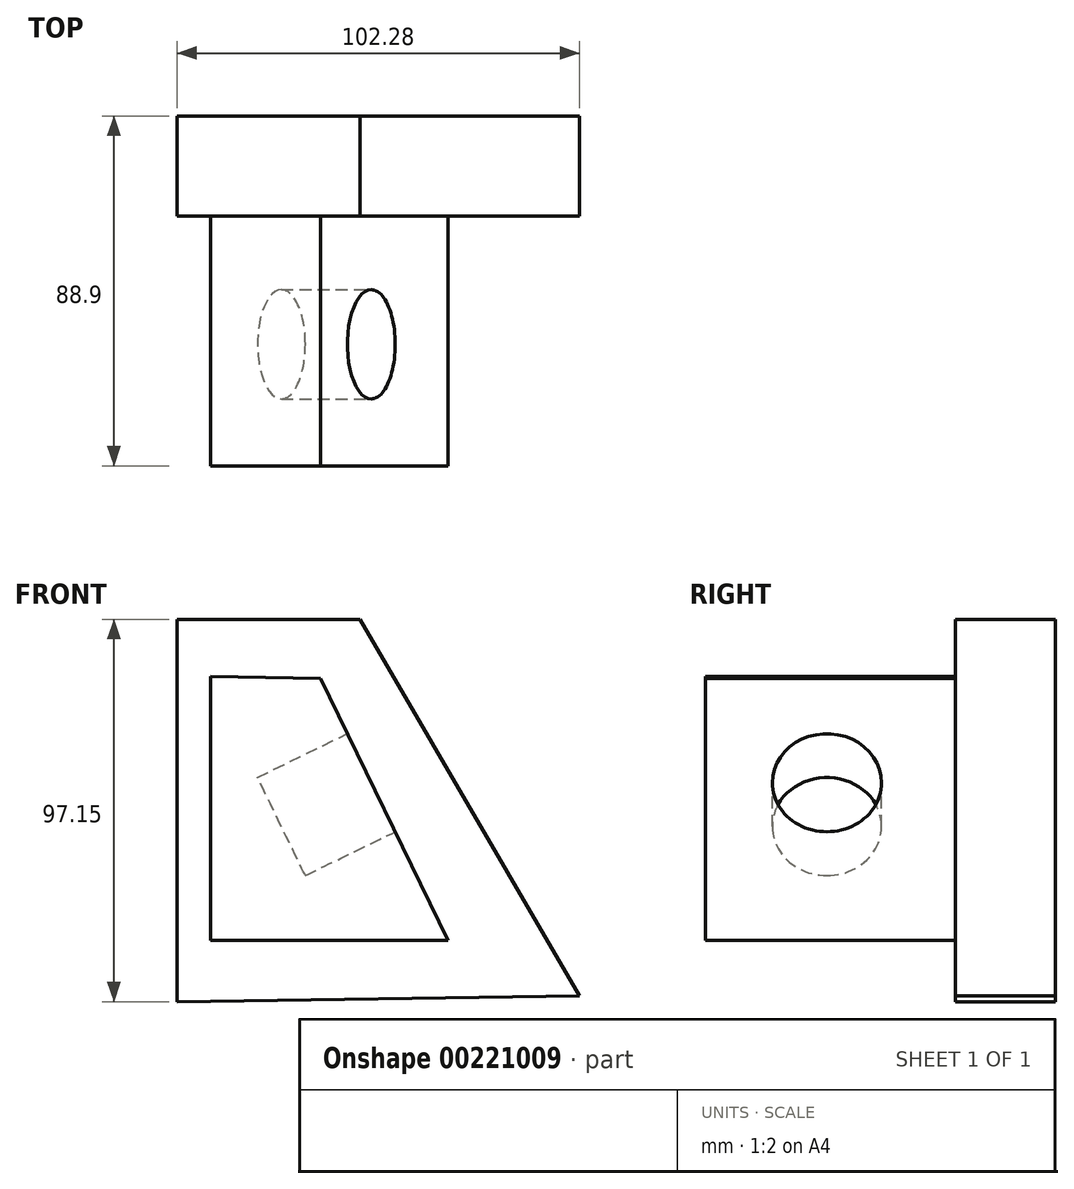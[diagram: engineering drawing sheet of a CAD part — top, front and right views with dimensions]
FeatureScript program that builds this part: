
annotation { "Feature Type Name" : "Feature", "Feature Type Description" : "" }
export const myFeature = defineFeature(function(context is Context, id is Id, definition is map)
    precondition{}
    {
        {
            var Q0;
            Q0=qCreatedBy(makeId("Front.planeOp"),FACE);
            var sketch = newSketch(context, id + "F0", { "sketchPlane" : qUnion([Q0])});
            skLineSegment(sketch, "E0", {"start": v(-58.29, 68.1) * mm, "end": v(-58.29, -29.05) * mm});
            skLineSegment(sketch, "E1", {"start": v(-58.29, 68.1) * mm, "end": v(-11.73, 68.1) * mm});
            skLineSegment(sketch, "E2", {"start": v(-11.73, 68.1) * mm, "end": v(44, -27.59) * mm});
            skLineSegment(sketch, "E3", {"start": v(44, -27.59) * mm, "end": v(-58.29, -29.05) * mm});
            skSolve(sketch);
        }
        {
            var Q0;
            Q0=makeQuery(id+"F0.imprint","IMPRINT",FACE,{"disambiguationData":[TD([[makeQuery(id+"F0.imprint","IMPRINT",EDGE,{"derivedFrom":sQuery(id+"F0.wireOp",EDGE,"E0")}),1.0]])]});
            extrude(context, id + "F1", {"entities" : qUnion([Q0]), "depth" : 25.4 * mm});
        }
        {
            var Q0;
            Q0=makeQuery(id+"F1.opExtrude","CAP_FACE",FACE,{"disambiguationData":[OSD([sQuery(id+"F0.wireOp",EDGE,"E0"),sQuery(id+"F0.wireOp",EDGE,"E1"),sQuery(id+"F0.wireOp",EDGE,"E2"),sQuery(id+"F0.wireOp",EDGE,"E3")])],"isStart":false});
            var sketch = newSketch(context, id + "F2", { "sketchPlane" : qUnion([Q0])});
            skLineSegment(sketch, "E4", {"start": v(-49.67, 53.61) * mm, "end": v(-49.67, -13.47) * mm});
            skLineSegment(sketch, "E5", {"start": v(10.63, -13.47) * mm, "end": v(-21.81, 53.07) * mm});
            skLineSegment(sketch, "E6", {"start": v(-21.81, 53.07) * mm, "end": v(-49.67, 53.61) * mm});
            skLineSegment(sketch, "E7", {"start": v(-49.67, -13.47) * mm, "end": v(10.63, -13.47) * mm});
            skSolve(sketch);
        }
        {
            var Q0;
            Q0=makeQuery(id+"F2.imprint","IMPRINT",FACE,{"disambiguationData":[TD([[makeQuery(id+"F2.imprint","IMPRINT",EDGE,{"derivedFrom":sQuery(id+"F2.wireOp",EDGE,"E4")}),1.0]])]});
            extrude(context, id + "F3", {"entities" : qUnion([Q0]), "operationType" : NewBodyOperationType.ADD, "depth" : 63.5 * mm});
        }
        {
            var Q0;
            Q0=makeQuery(id+"F3.opExtrude","SWEPT_FACE",FACE,{"disambiguationData":[OSD([sQuery(id+"F2.wireOp",EDGE,"E5")])]});
            var sketch = newSketch(context, id + "F4", { "sketchPlane" : qUnion([Q0])});
            skSolve(sketch);
        }
        {
            var Q0;
            {var subQ0=sQuery(id+"F2.wireOp",EDGE,"E5");Q0=makeQuery(id+"F4.imprint","IMPRINT",FACE,{"disambiguationData":[TD([[makeQuery(id+"F4.imprint","IMPRINT",EDGE,{"derivedFrom":makeQuery(id+"F3.opExtrude","CAP_EDGE",EDGE,{"disambiguationData":[OSD([subQ0])],"isStart":false})}),-1.0]])]});}
            var sketch = newSketch(context, id + "F5", { "sketchPlane" : qUnion([Q0])});
            skCircle(sketch, "E8", {"center": v(-58.03, 27.8) * mm, "radius": 13.86 * mm});
            skPoint(sketch, "E8.first.point", {"position": v(-60.12, 14.09) * mm});
            skPoint(sketch, "E8.second.point", {"position": v(-55.1, 41.34) * mm});
            skPoint(sketch, "E8.third.point", {"position": v(-45.13, 32.88) * mm});
            skSolve(sketch);
        }
        {
            var Q0;
            Q0=makeQuery(id+"F5.imprint","IMPRINT",FACE,{"disambiguationData":[TD([[makeQuery(id+"F5.imprint","IMPRINT",EDGE,{"derivedFrom":sQuery(id+"F5.wireOp",EDGE,"E8")}),1.0]])]});
            extrude(context, id + "F6", {"entities" : qUnion([Q0]), "operationType" : NewBodyOperationType.REMOVE, "oppositeDirection" : true, "depth" : 25.4 * mm});
        }
    });
